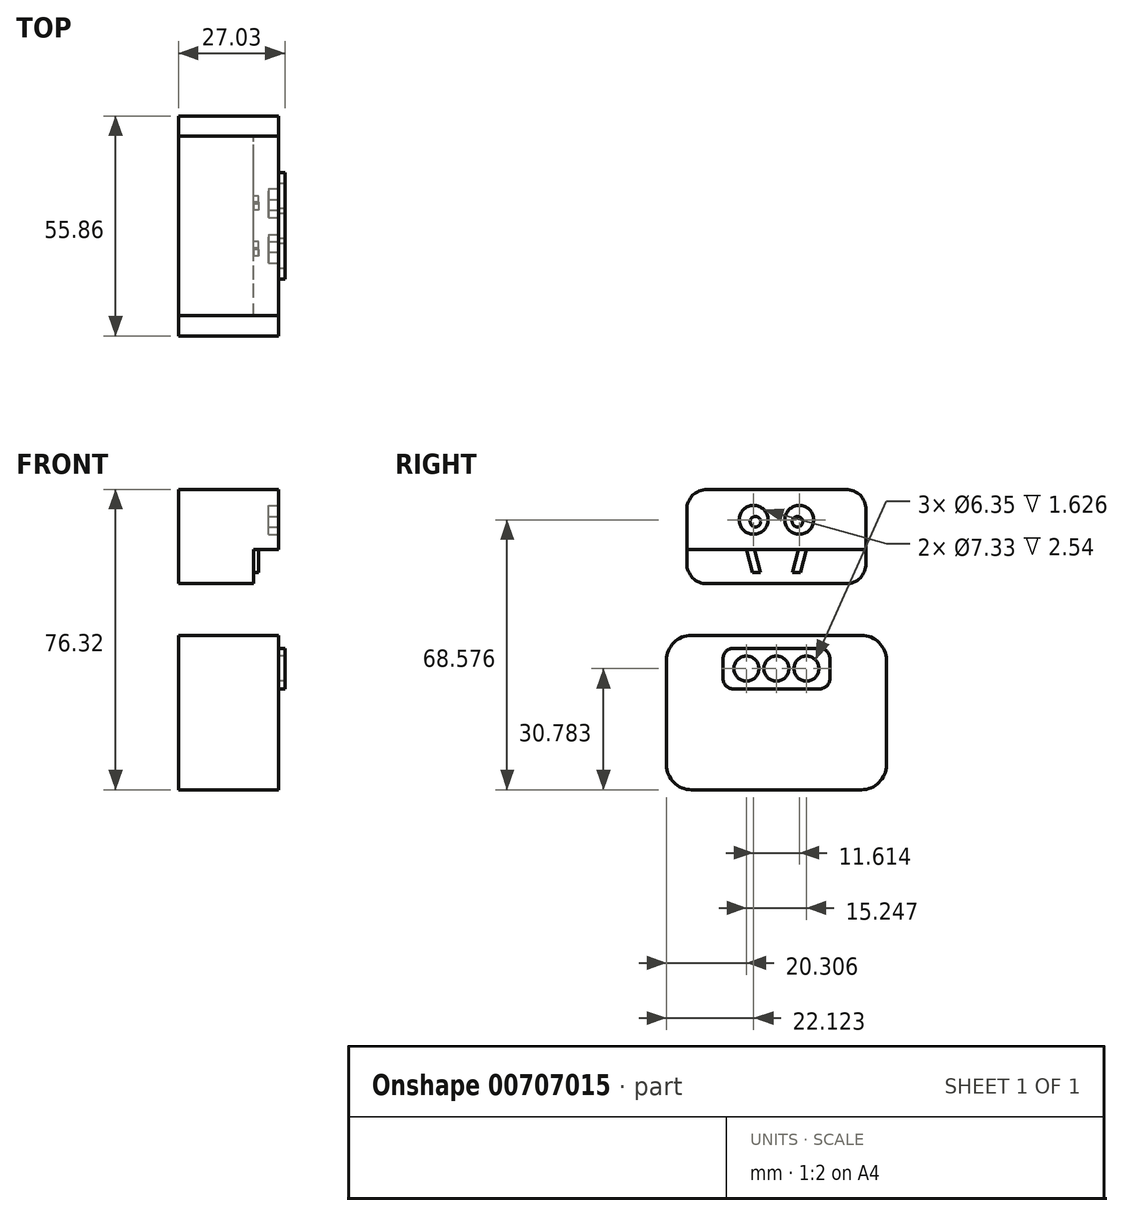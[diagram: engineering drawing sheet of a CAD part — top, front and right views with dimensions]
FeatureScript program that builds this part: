
annotation { "Feature Type Name" : "Feature", "Feature Type Description" : "" }
export const myFeature = defineFeature(function(context is Context, id is Id, definition is map)
    precondition{}
    {
        {
            var Q0;
            Q0=qCreatedBy(makeId("Right.planeOp"),FACE);
            var sketch = newSketch(context, id + "F0", { "sketchPlane" : qUnion([Q0])});
            skLineSegment(sketch, "E0.bottom", {"start": v(21.58, -19.63) * mm, "end": v(-21.58, -19.63) * mm});
            skLineSegment(sketch, "E0.top", {"start": v(21.58, 19.63) * mm, "end": v(-21.58, 19.63) * mm});
            skLineSegment(sketch, "E0.left", {"start": v(27.93, -13.28) * mm, "end": v(27.93, 13.28) * mm});
            skLineSegment(sketch, "E0.right", {"start": v(-27.93, -13.28) * mm, "end": v(-27.93, 13.28) * mm});
            skPoint(sketch, "E0.middle", {"position": v(0, 0) * mm});
            skPoint(sketch, "E1.visualSharp", {"position": v(-27.93, 19.63) * mm});
            skArc(sketch, "E1.filletArc", {"start": v(-21.58, 19.63) * mm, "mid": v(-26.07, 17.77) * mm, "end": v(-27.93, 13.28) * mm});
            skPoint(sketch, "E2.visualSharp", {"position": v(27.93, 19.63) * mm});
            skArc(sketch, "E2.filletArc", {"start": v(27.93, 13.28) * mm, "mid": v(26.07, 17.77) * mm, "end": v(21.58, 19.63) * mm});
            skPoint(sketch, "E3.visualSharp", {"position": v(27.93, -19.63) * mm});
            skArc(sketch, "E3.filletArc", {"start": v(21.58, -19.63) * mm, "mid": v(26.07, -17.77) * mm, "end": v(27.93, -13.28) * mm});
            skLineSegment(sketch, "E4.bottom", {"start": v(12.58, 6.25) * mm, "end": v(-12.58, 6.25) * mm});
            skLineSegment(sketch, "E4.top", {"start": v(12.58, 15.62) * mm, "end": v(-12.58, 15.62) * mm});
            skLineSegment(sketch, "E4.left", {"start": v(15.12, 8.8) * mm, "end": v(15.12, 13.08) * mm});
            skLineSegment(sketch, "E4.right", {"start": v(-15.12, 8.8) * mm, "end": v(-15.12, 13.08) * mm});
            skPoint(sketch, "E4.middle", {"position": v(0, 10.94) * mm});
            skPoint(sketch, "E5.visualSharp", {"position": v(-15.12, 15.62) * mm});
            skArc(sketch, "E5.filletArc", {"start": v(-12.58, 15.62) * mm, "mid": v(-14.38, 14.87) * mm, "end": v(-15.12, 13.08) * mm});
            skPoint(sketch, "E6.visualSharp", {"position": v(15.12, 15.62) * mm});
            skArc(sketch, "E6.filletArc", {"start": v(15.12, 13.08) * mm, "mid": v(14.38, 14.87) * mm, "end": v(12.58, 15.62) * mm});
            skPoint(sketch, "E7.visualSharp", {"position": v(15.12, 6.25) * mm});
            skArc(sketch, "E7.filletArc", {"start": v(12.58, 6.25) * mm, "mid": v(14.38, 7) * mm, "end": v(15.12, 8.8) * mm});
            skPoint(sketch, "E8.visualSharp", {"position": v(-15.12, 6.25) * mm});
            skArc(sketch, "E8.filletArc", {"start": v(-15.12, 8.8) * mm, "mid": v(-14.38, 7) * mm, "end": v(-12.58, 6.25) * mm});
            skPoint(sketch, "E9.visualSharp", {"position": v(-27.93, -19.63) * mm});
            skArc(sketch, "E9.filletArc", {"start": v(-27.93, -13.28) * mm, "mid": v(-26.07, -17.77) * mm, "end": v(-21.58, -19.63) * mm});
            skSolve(sketch);
        }
        {
            var Q0;
            Q0=makeQuery(id+"F0.imprint","IMPRINT",FACE,{"disambiguationData":[TD([[makeQuery(id+"F0.imprint","IMPRINT",EDGE,{"derivedFrom":sQuery(id+"F0.wireOp",EDGE,"E0.bottom")}),-1.0]])]});
            var Q1;
            Q1=makeQuery(id+"F0.imprint","IMPRINT",FACE,{"disambiguationData":[TD([[makeQuery(id+"F0.imprint","IMPRINT",EDGE,{"derivedFrom":sQuery(id+"F0.wireOp",EDGE,"E4.bottom")}),-1.0]])]});
            extrude(context, id + "F1", {"entities" : qUnion([Q0, Q1]), "depth" : 25.4 * mm, "offsetDistance" : 25.4 * mm});
        }
        {
            var Q0;
            Q0=makeQuery(id+"F1.opExtrude","CAP_FACE",FACE,{"disambiguationData":[OSD([sQuery(id+"F0.wireOp",EDGE,"E0.bottom"),sQuery(id+"F0.wireOp",EDGE,"E0.top"),sQuery(id+"F0.wireOp",EDGE,"E0.left"),sQuery(id+"F0.wireOp",EDGE,"E0.right"),sQuery(id+"F0.wireOp",EDGE,"E1.filletArc"),sQuery(id+"F0.wireOp",EDGE,"E2.filletArc"),sQuery(id+"F0.wireOp",EDGE,"E3.filletArc"),sQuery(id+"F0.wireOp",EDGE,"E9.filletArc")])],"isStart":false});
            var sketch = newSketch(context, id + "F2", { "sketchPlane" : qUnion([Q0])});
            skLineSegment(sketch, "E10.bottom", {"start": v(11.01, 6) * mm, "end": v(-11.01, 6) * mm});
            skLineSegment(sketch, "E10.top", {"start": v(11.01, 16.32) * mm, "end": v(-11.01, 16.32) * mm});
            skLineSegment(sketch, "E10.left", {"start": v(13.55, 8.53) * mm, "end": v(13.55, 13.78) * mm});
            skLineSegment(sketch, "E10.right", {"start": v(-13.55, 8.53) * mm, "end": v(-13.55, 13.78) * mm});
            skPoint(sketch, "E10.middle", {"position": v(0, 11.15) * mm});
            skPoint(sketch, "E11.visualSharp", {"position": v(-13.55, 6) * mm});
            skArc(sketch, "E11.filletArc", {"start": v(-13.55, 8.53) * mm, "mid": v(-12.8, 6.74) * mm, "end": v(-11.01, 6) * mm});
            skPoint(sketch, "E12.visualSharp", {"position": v(13.55, 6) * mm});
            skArc(sketch, "E12.filletArc", {"start": v(11.01, 6) * mm, "mid": v(12.8, 6.74) * mm, "end": v(13.55, 8.53) * mm});
            skPoint(sketch, "E13.visualSharp", {"position": v(13.55, 16.32) * mm});
            skArc(sketch, "E13.filletArc", {"start": v(13.55, 13.78) * mm, "mid": v(12.8, 15.57) * mm, "end": v(11.01, 16.32) * mm});
            skPoint(sketch, "E14.visualSharp", {"position": v(-13.55, 16.32) * mm});
            skArc(sketch, "E14.filletArc", {"start": v(-11.01, 16.32) * mm, "mid": v(-12.8, 15.57) * mm, "end": v(-13.55, 13.78) * mm});
            skCircle(sketch, "E15", {"center": v(0, 11.15) * mm, "radius": 3.18 * mm});
            skCircle(sketch, "E16", {"center": v(7.62, 11.15) * mm, "radius": 3.18 * mm});
            skLineSegment(sketch, "E17", {"start": v(0, 16.32) * mm, "end": v(0, 6) * mm, "construction": true});
            skCircle(sketch, "E18.MirrorC", {"center": v(-7.62, 11.15) * mm, "radius": 3.18 * mm});
            skSolve(sketch);
        }
        {
            var Q0;
            Q0 = qSketchRegion(id + "F2", true);
            extrude(context, id + "F3", {"entities" : qUnion([Q0]), "operationType" : NewBodyOperationType.ADD, "depth" : 1.63 * mm, "offsetDistance" : 25.4 * mm});
        }
        {
            var Q0;
            Q0=qCreatedBy(makeId("Right.planeOp"),FACE);
            var sketch = newSketch(context, id + "F4", { "sketchPlane" : qUnion([Q0])});
            skLineSegment(sketch, "E19.bottom", {"start": v(17.69, 32.72) * mm, "end": v(-17.69, 32.72) * mm});
            skLineSegment(sketch, "E19.top", {"start": v(17.69, 56.69) * mm, "end": v(-17.69, 56.69) * mm});
            skLineSegment(sketch, "E19.left", {"start": v(22.77, 37.8) * mm, "end": v(22.77, 51.6) * mm});
            skLineSegment(sketch, "E19.right", {"start": v(-22.77, 37.8) * mm, "end": v(-22.77, 51.6) * mm});
            skPoint(sketch, "E19.middle", {"position": v(0, 44.7) * mm});
            skPoint(sketch, "E20.visualSharp", {"position": v(-22.77, 56.69) * mm});
            skArc(sketch, "E20.filletArc", {"start": v(-17.69, 56.69) * mm, "mid": v(-21.28, 55.2) * mm, "end": v(-22.77, 51.6) * mm});
            skPoint(sketch, "E21.visualSharp", {"position": v(22.77, 56.69) * mm});
            skArc(sketch, "E21.filletArc", {"start": v(22.77, 51.6) * mm, "mid": v(21.28, 55.2) * mm, "end": v(17.69, 56.69) * mm});
            skPoint(sketch, "E22.visualSharp", {"position": v(22.77, 32.72) * mm});
            skArc(sketch, "E22.filletArc", {"start": v(17.69, 32.72) * mm, "mid": v(21.28, 34.21) * mm, "end": v(22.77, 37.8) * mm});
            skPoint(sketch, "E23.visualSharp", {"position": v(-22.77, 32.72) * mm});
            skArc(sketch, "E23.filletArc", {"start": v(-22.77, 37.8) * mm, "mid": v(-21.28, 34.21) * mm, "end": v(-17.69, 32.72) * mm});
            skSolve(sketch);
        }
        {
            var Q0;
            Q0 = qSketchRegion(id + "F4", true);
            extrude(context, id + "F5", {"entities" : qUnion([Q0]), "depth" : 25.4 * mm, "offsetDistance" : 25.4 * mm});
        }
        {
            var Q0;
            Q0=makeQuery(id+"F5.opExtrude","CAP_FACE",FACE,{"disambiguationData":[OSD([sQuery(id+"F4.wireOp",EDGE,"E19.bottom"),sQuery(id+"F4.wireOp",EDGE,"E19.top"),sQuery(id+"F4.wireOp",EDGE,"E19.left"),sQuery(id+"F4.wireOp",EDGE,"E19.right"),sQuery(id+"F4.wireOp",EDGE,"E20.filletArc"),sQuery(id+"F4.wireOp",EDGE,"E21.filletArc"),sQuery(id+"F4.wireOp",EDGE,"E22.filletArc"),sQuery(id+"F4.wireOp",EDGE,"E23.filletArc")])],"isStart":false});
            var sketch = newSketch(context, id + "F6", { "sketchPlane" : qUnion([Q0])});
            skCircle(sketch, "E24", {"center": v(-5.8, 48.95) * mm, "radius": 3.67 * mm});
            skLineSegment(sketch, "E25", {"start": v(0, 56.69) * mm, "end": v(0, 32.72) * mm, "construction": true});
            skLineSegment(sketch, "E26", {"start": v(0, 32.72) * mm, "end": v(0, 32.72) * mm});
            skCircle(sketch, "E27.MirrorC", {"center": v(5.8, 48.95) * mm, "radius": 3.67 * mm});
            skCircle(sketch, "E28", {"center": v(-5.34, 48.49) * mm, "radius": 1.34 * mm});
            skCircle(sketch, "E29.MirrorC", {"center": v(5.34, 48.49) * mm, "radius": 1.34 * mm});
            skSolve(sketch);
        }
        {
            var Q0;
            Q0 = qSketchRegion(id + "F6", true);
            extrude(context, id + "F7", {"entities" : qUnion([Q0]), "operationType" : NewBodyOperationType.REMOVE, "oppositeDirection" : true, "depth" : 2.54 * mm, "offsetDistance" : 25.4 * mm});
        }
        {
            var Q0;
            {var subQ0=sQuery(id+"F4.wireOp",EDGE,"E19.left");var subQ1=sQuery(id+"F4.wireOp",EDGE,"E19.top");var subQ2=sQuery(id+"F4.wireOp",EDGE,"E19.right");var subQ3=sQuery(id+"F4.wireOp",EDGE,"E19.bottom");var subQ4=sQuery(id+"F4.wireOp",EDGE,"E20.filletArc");var subQ5=sQuery(id+"F4.wireOp",EDGE,"E21.filletArc");var subQ6=sQuery(id+"F4.wireOp",EDGE,"E22.filletArc");var subQ7=sQuery(id+"F4.wireOp",EDGE,"E23.filletArc");Q0=makeQuery(id+"F7.boolean.opBoolean","SPLIT",FACE,{"disambiguationData":[TD([makeQuery(id+"F5.opExtrude","SWEPT_FACE",FACE,{"disambiguationData":[OSD([subQ3])]})])],"derivedFrom":makeQuery(id+"F5.opExtrude","CAP_FACE",FACE,{"disambiguationData":[OSD([subQ3,subQ1,subQ0,subQ2,subQ4,subQ5,subQ6,subQ7])],"isStart":false})});}
            var sketch = newSketch(context, id + "F8", { "sketchPlane" : qUnion([Q0])});
            skLineSegment(sketch, "E30.bottom", {"start": v(-24.41, 41.39) * mm, "end": v(24.38, 41.39) * mm});
            skLineSegment(sketch, "E30.top", {"start": v(-24.41, 32.72) * mm, "end": v(24.38, 32.72) * mm});
            skLineSegment(sketch, "E30.left", {"start": v(-24.41, 41.39) * mm, "end": v(-24.41, 32.72) * mm});
            skLineSegment(sketch, "E30.right", {"start": v(24.38, 41.39) * mm, "end": v(24.38, 32.72) * mm});
            skSolve(sketch);
        }
        {
            var Q0;
            Q0 = qSketchRegion(id + "F8", true);
            extrude(context, id + "F9", {"entities" : qUnion([Q0]), "operationType" : NewBodyOperationType.REMOVE, "oppositeDirection" : true, "depth" : 6.35 * mm, "offsetDistance" : 25.4 * mm});
        }
        {
            var Q0;
            Q0=makeQuery(id+"F9.boolean.opBoolean","COPY",FACE,{"derivedFrom":makeQuery(id+"F9.opExtrude","CAP_FACE",FACE,{"disambiguationData":[OSD([sQuery(id+"F8.wireOp",EDGE,"E30.bottom"),sQuery(id+"F8.wireOp",EDGE,"E30.top"),sQuery(id+"F8.wireOp",EDGE,"E30.left"),sQuery(id+"F8.wireOp",EDGE,"E30.right")])],"isStart":false})});
            var sketch = newSketch(context, id + "F10", { "sketchPlane" : qUnion([Q0])});
            skLineSegment(sketch, "E31", {"start": v(0, 32.72) * mm, "end": v(0, 41.39) * mm});
            skLineSegment(sketch, "E32", {"start": v(-6.05, 35.6) * mm, "end": v(0, 35.6) * mm});
            skLineSegment(sketch, "E33.MirrorCS", {"start": v(6.05, 35.6) * mm, "end": v(0, 35.6) * mm});
            skLineSegment(sketch, "E34", {"start": v(-1.99, 35.6) * mm, "end": v(-3.55, 41.39) * mm});
            skPoint(sketch, "E34.endSnap0", {"position": v(-3.55, 35.69) * mm});
            skLineSegment(sketch, "E35", {"start": v(-6.05, 35.6) * mm, "end": v(-7.61, 41.39) * mm});
            skLineSegment(sketch, "E36", {"start": v(-5.58, 41.39) * mm, "end": v(-4.02, 35.6) * mm});
            skLineSegment(sketch, "E37.MirrorCS", {"start": v(1.99, 35.6) * mm, "end": v(3.55, 41.39) * mm});
            skLineSegment(sketch, "E38.MirrorCS", {"start": v(5.58, 41.39) * mm, "end": v(4.02, 35.6) * mm});
            skLineSegment(sketch, "E39.MirrorCS", {"start": v(6.05, 35.6) * mm, "end": v(7.61, 41.39) * mm});
            skLineSegment(sketch, "E40", {"start": v(-7.61, 41.39) * mm, "end": v(0, 41.39) * mm});
            skLineSegment(sketch, "E41", {"start": v(0, 41.39) * mm, "end": v(7.61, 41.39) * mm});
            skSolve(sketch);
        }
        {
            var Q0;
            {var subQ2=sQuery(id+"F10.wireOp",EDGE,"E38.MirrorCS");Q0=makeQuery(id+"F10.imprint","IMPRINT",FACE,{"disambiguationData":[TD([[makeQuery(id+"F10.imprint","IMPRINT",EDGE,{"derivedFrom":subQ2}),1.0]])]});}
            var Q1;
            {var subQ0=sQuery(id+"F10.wireOp",EDGE,"E35");Q1=makeQuery(id+"F10.imprint","IMPRINT",FACE,{"disambiguationData":[TD([[makeQuery(id+"F10.imprint","IMPRINT",EDGE,{"derivedFrom":subQ0}),-1.0]])]});}
            extrude(context, id + "F11", {"entities" : qUnion([Q0, Q1]), "operationType" : NewBodyOperationType.ADD, "depth" : 1.27 * mm, "offsetDistance" : 25.4 * mm});
        }
    });
